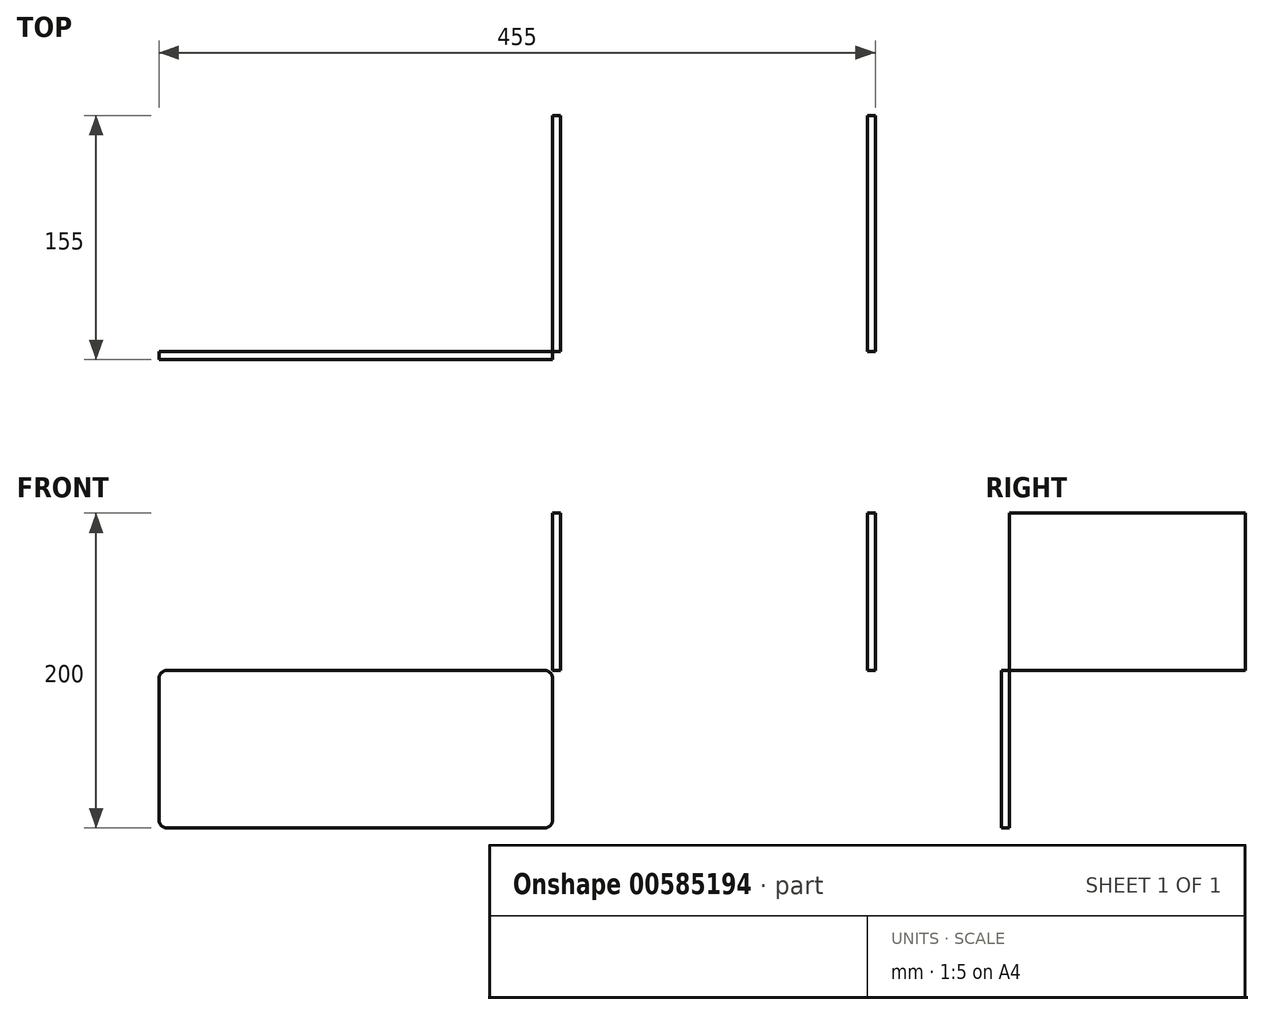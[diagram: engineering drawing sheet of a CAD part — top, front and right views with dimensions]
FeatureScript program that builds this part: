
annotation { "Feature Type Name" : "Feature", "Feature Type Description" : "" }
export const myFeature = defineFeature(function(context is Context, id is Id, definition is map)
    precondition{}
    {
        {
            var Q0;
            Q0=qCreatedBy(makeId("Front.planeOp"),FACE);
            var sketch = newSketch(context, id + "F0", { "sketchPlane" : qUnion([Q0])});
            skLineSegment(sketch, "E0.bottom", {"start": v(-250, 0) * mm, "end": v(0, 0) * mm});
            skLineSegment(sketch, "E0.top", {"start": v(-250, -100) * mm, "end": v(0, -100) * mm});
            skLineSegment(sketch, "E0.left", {"start": v(-250, 0) * mm, "end": v(-250, -100) * mm});
            skLineSegment(sketch, "E0.right", {"start": v(0, 0) * mm, "end": v(0, -100) * mm});
            skSolve(sketch);
        }
        {
            var Q0;
            Q0=makeQuery(id+"F0.imprint","IMPRINT",FACE,{"disambiguationData":[TD([[makeQuery(id+"F0.imprint","IMPRINT",EDGE,{"derivedFrom":sQuery(id+"F0.wireOp",EDGE,"E0.bottom")}),-1.0]])]});
            extrude(context, id + "F1", {"entities" : qUnion([Q0]), "depth" : 5 * mm, "offsetDistance" : 25 * mm});
        }
        {
            var Q0;
            Q0=makeQuery(id+"F1.opExtrude","SWEPT_EDGE",EDGE,{"disambiguationData":[OSD([sQuery(id+"F0.wireOp",EDGE,"E0.top"),sQuery(id+"F0.wireOp",EDGE,"E0.left")])]});
            var Q1;
            Q1=makeQuery(id+"F1.opExtrude","SWEPT_EDGE",EDGE,{"disambiguationData":[OSD([sQuery(id+"F0.wireOp",EDGE,"E0.top"),sQuery(id+"F0.wireOp",EDGE,"E0.right")])]});
            var Q2;
            Q2=makeQuery(id+"F1.opExtrude","SWEPT_EDGE",EDGE,{"disambiguationData":[OSD([sQuery(id+"F0.wireOp",EDGE,"E0.bottom"),sQuery(id+"F0.wireOp",EDGE,"E0.right")])]});
            var Q3;
            Q3=makeQuery(id+"F1.opExtrude","SWEPT_EDGE",EDGE,{"disambiguationData":[OSD([sQuery(id+"F0.wireOp",EDGE,"E0.bottom"),sQuery(id+"F0.wireOp",EDGE,"E0.left")])]});
            fillet(context, id + "F2", {"entities" : qUnion([Q0, Q1, Q2, Q3]), "radius" : 5 * mm, "tangentPropagation" : true, "allowEdgeOverflow" : false});
        }
        {
            var Q0;
            Q0=qCreatedBy(makeId("Right.planeOp"),FACE);
            var sketch = newSketch(context, id + "F3", { "sketchPlane" : qUnion([Q0])});
            skLineSegment(sketch, "E1.bottom", {"start": v(0, 100) * mm, "end": v(150, 100) * mm});
            skLineSegment(sketch, "E1.top", {"start": v(0, 0) * mm, "end": v(150, 0) * mm});
            skLineSegment(sketch, "E1.left", {"start": v(0, 100) * mm, "end": v(0, 0) * mm});
            skLineSegment(sketch, "E1.right", {"start": v(150, 100) * mm, "end": v(150, 0) * mm});
            skSolve(sketch);
        }
        {
            var Q0;
            Q0=makeQuery(id+"F3.imprint","IMPRINT",FACE,{"disambiguationData":[TD([[makeQuery(id+"F3.imprint","IMPRINT",EDGE,{"derivedFrom":sQuery(id+"F3.wireOp",EDGE,"E1.bottom")}),-1.0]])]});
            extrude(context, id + "F4", {"entities" : qUnion([Q0]), "depth" : 5 * mm, "offsetDistance" : 25 * mm});
        }
        {
            var Q0;
            Q0=makeQuery(id+"F4.opExtrude","SWEPT_BODY",BODY,{"disambiguationData":[OSD([sQuery(id+"F3.wireOp",EDGE,"E1.bottom"),sQuery(id+"F3.wireOp",EDGE,"E1.top"),sQuery(id+"F3.wireOp",EDGE,"E1.left"),sQuery(id+"F3.wireOp",EDGE,"E1.right")])]});
            transform(context, id + "F5", {"entities" : qUnion([Q0]), "transformType" : TransformType.TRANSLATION_3D, "dx" : 200 * mm, "dy" : 0 * mm, "dz" : 0 * mm, "makeCopy" : true});
        }
    });
